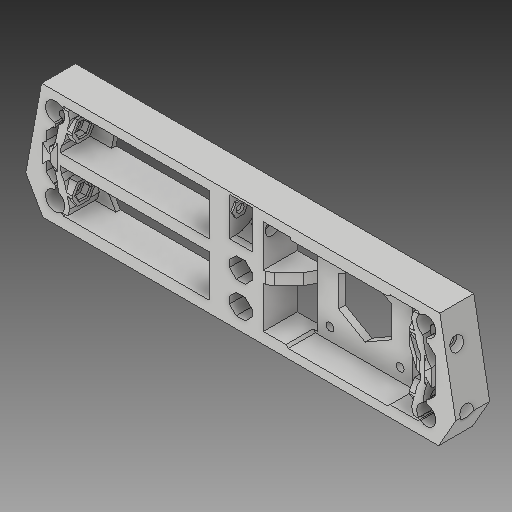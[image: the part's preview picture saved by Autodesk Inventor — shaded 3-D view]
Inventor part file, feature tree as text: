
AUTODESK INVENTOR PART (.ipt)
format: ipt  version: 2017 (Build 210142000, 142)  size: 564,736 bytes
history: native  units: in
note: dims shown in document units (in); Inventor stores cm internally (conversion verified against a paired STEP export)
features: fillet x1
ambient origin geometry x8: Origin, YZ Plane, XZ Plane, XY Plane, X Axis, Y Axis, Z Axis, Center Point
bodies: Solid1 (feature_tree)
feature tree (1):
  fillet  "Congé6"  [1 undecoded]
note: 1 required parameter value undecoded (feature->parameter linkage not recoverable at this tier; creation-order binding heuristic only, values carry confidence <= 0.55)
